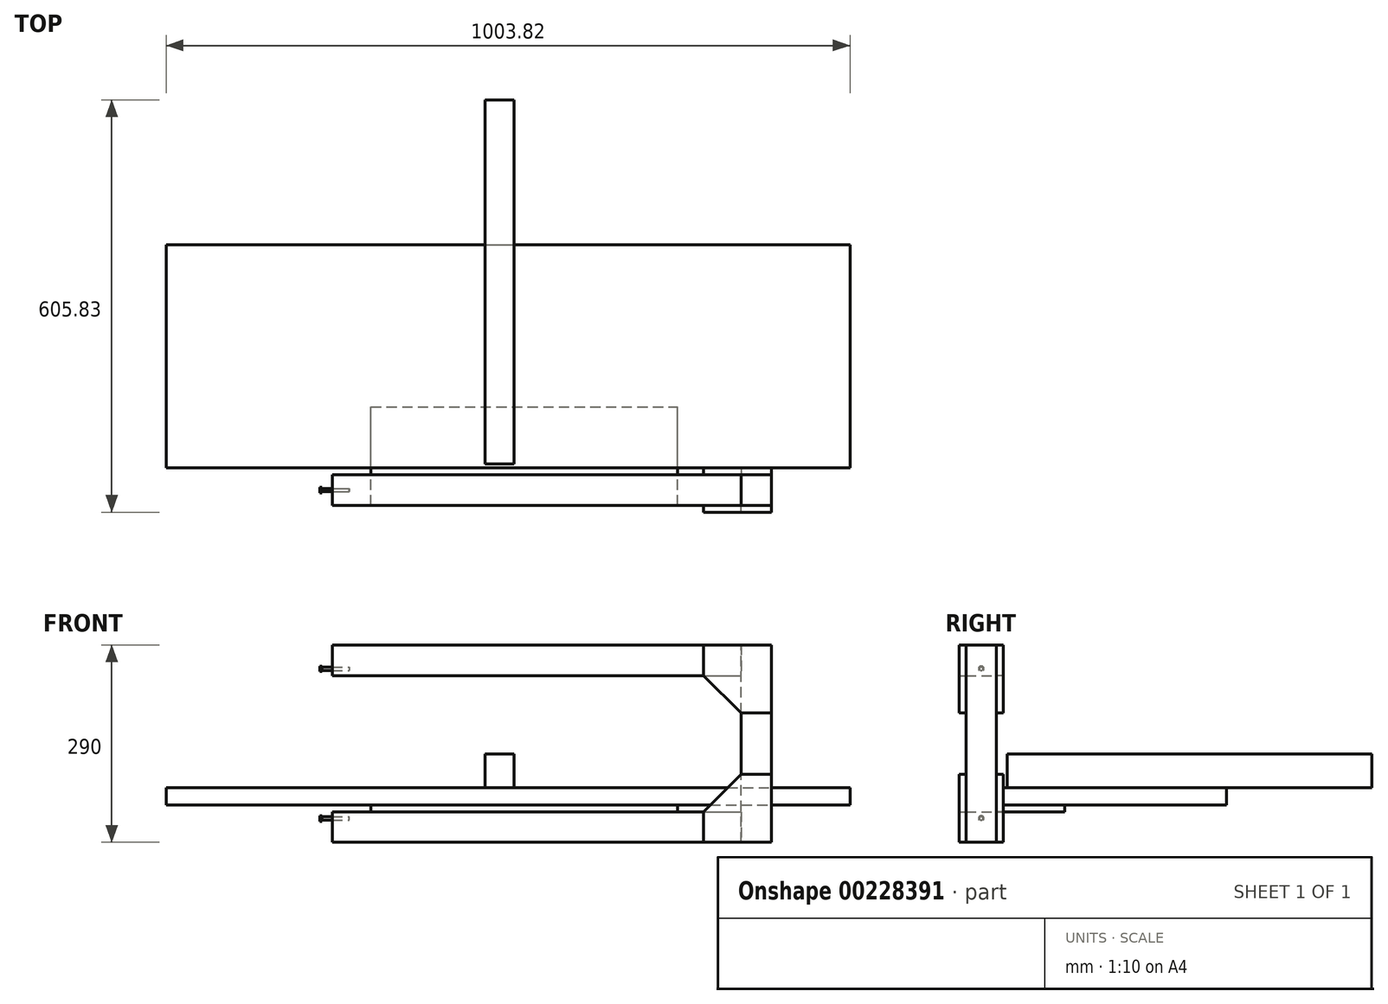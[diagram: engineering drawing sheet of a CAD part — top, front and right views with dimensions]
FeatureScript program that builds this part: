
annotation { "Feature Type Name" : "Feature", "Feature Type Description" : "" }
export const myFeature = defineFeature(function(context is Context, id is Id, definition is map)
    precondition{}
    {
        {
            var Q0;
            Q0=qCreatedBy(makeId("Front.planeOp"),FACE);
            var sketch = newSketch(context, id + "F0", { "sketchPlane" : qUnion([Q0])});
            skLineSegment(sketch, "E0.bottom", {"start": v(22.5, -145) * mm, "end": v(-22.5, -145) * mm});
            skLineSegment(sketch, "E0.top", {"start": v(22.5, 145) * mm, "end": v(-22.5, 145) * mm});
            skLineSegment(sketch, "E0.left", {"start": v(22.5, -145) * mm, "end": v(22.5, 145) * mm});
            skLineSegment(sketch, "E0.right", {"start": v(-22.5, -145) * mm, "end": v(-22.5, 145) * mm});
            skPoint(sketch, "E0.middle", {"position": v(0, 0) * mm});
            skSolve(sketch);
        }
        {
            var Q0;
            Q0 = qSketchRegion(id + "F0", true);
            extrude(context, id + "F1", {"entities" : qUnion([Q0]), "endBound" : BoundingType.SYMMETRIC, "depth" : 45 * mm});
        }
        {
            var Q0;
            Q0=qCreatedBy(makeId("Front.planeOp"),FACE);
            var sketch = newSketch(context, id + "F2", { "sketchPlane" : qUnion([Q0])});
            skLineSegment(sketch, "E1.bottom", {"start": v(-622.5, 145) * mm, "end": v(-22.5, 145) * mm});
            skLineSegment(sketch, "E1.top", {"start": v(-622.5, 100) * mm, "end": v(-22.5, 100) * mm});
            skLineSegment(sketch, "E1.left", {"start": v(-622.5, 145) * mm, "end": v(-622.5, 100) * mm});
            skLineSegment(sketch, "E1.right", {"start": v(-22.5, 145) * mm, "end": v(-22.5, 100) * mm});
            skLineSegment(sketch, "E2.bottom", {"start": v(-622.5, -100) * mm, "end": v(-22.5, -100) * mm});
            skLineSegment(sketch, "E2.top", {"start": v(-622.5, -145) * mm, "end": v(-22.5, -145) * mm});
            skLineSegment(sketch, "E2.left", {"start": v(-622.5, -100) * mm, "end": v(-622.5, -145) * mm});
            skLineSegment(sketch, "E2.right", {"start": v(-22.5, -100) * mm, "end": v(-22.5, -145) * mm});
            skSolve(sketch);
        }
        {
            var Q0;
            Q0 = qSketchRegion(id + "F2", true);
            extrude(context, id + "F3", {"entities" : qUnion([Q0]), "endBound" : BoundingType.SYMMETRIC, "depth" : 45 * mm});
        }
        {
            var Q0;
            Q0=makeQuery(id+"F1.opExtrude","CAP_FACE",FACE,{"disambiguationData":[OSD([sQuery(id+"F0.wireOp",EDGE,"E0.bottom"),sQuery(id+"F0.wireOp",EDGE,"E0.top"),sQuery(id+"F0.wireOp",EDGE,"E0.left"),sQuery(id+"F0.wireOp",EDGE,"E0.right")])],"isStart":false});
            var sketch = newSketch(context, id + "F4", { "sketchPlane" : qUnion([Q0])});
            skLineSegment(sketch, "E3", {"start": v(22.5, -145) * mm, "end": v(22.5, -45) * mm});
            skLineSegment(sketch, "E4", {"start": v(22.5, -45) * mm, "end": v(-22.5, -45) * mm});
            skLineSegment(sketch, "E5", {"start": v(-22.5, -45) * mm, "end": v(-77.5, -100) * mm});
            skLineSegment(sketch, "E6", {"start": v(-77.5, -100) * mm, "end": v(-77.5, -145) * mm});
            skLineSegment(sketch, "E7", {"start": v(-77.5, -145) * mm, "end": v(22.5, -145) * mm});
            skSolve(sketch);
        }
        {
            var Q0;
            Q0 = qSketchRegion(id + "F4", true);
            extrude(context, id + "F5", {"entities" : qUnion([Q0]), "depth" : 10 * mm});
        }
        {
            var Q0;
            Q0=makeQuery(id+"F5.opExtrude","SWEPT_BODY",BODY,{"disambiguationData":[OSD([sQuery(id+"F4.wireOp",EDGE,"E3"),sQuery(id+"F4.wireOp",EDGE,"E4"),sQuery(id+"F4.wireOp",EDGE,"E5"),sQuery(id+"F4.wireOp",EDGE,"E6"),sQuery(id+"F4.wireOp",EDGE,"E7")])]});
            var Q1;
            Q1=qCreatedBy(makeId("Front.planeOp"),FACE);
            mirror(context, id + "F6", {"entities" : qUnion([Q0]), "mirrorPlane" : qUnion([Q1])});
        }
        {
            var Q0;
            Q0=makeQuery(id+"F5.opExtrude","SWEPT_BODY",BODY,{"disambiguationData":[OSD([sQuery(id+"F4.wireOp",EDGE,"E3"),sQuery(id+"F4.wireOp",EDGE,"E4"),sQuery(id+"F4.wireOp",EDGE,"E5"),sQuery(id+"F4.wireOp",EDGE,"E6"),sQuery(id+"F4.wireOp",EDGE,"E7")])]});
            var Q1;
            Q1=makeQuery(id+"F6.opPattern","COPY",BODY,{"derivedFrom":makeQuery(id+"F5.opExtrude","SWEPT_BODY",BODY,{"disambiguationData":[OSD([sQuery(id+"F4.wireOp",EDGE,"E3"),sQuery(id+"F4.wireOp",EDGE,"E4"),sQuery(id+"F4.wireOp",EDGE,"E5"),sQuery(id+"F4.wireOp",EDGE,"E6"),sQuery(id+"F4.wireOp",EDGE,"E7")])]}),"instanceName":"1"});
            var Q2;
            Q2=qCreatedBy(makeId("Top.planeOp"),FACE);
            mirror(context, id + "F7", {"entities" : qUnion([Q0, Q1]), "mirrorPlane" : qUnion([Q2])});
        }
        {
            var Q0;
            Q0=makeQuery(id+"F3.opExtrude","SWEPT_FACE",FACE,{"disambiguationData":[OSD([sQuery(id+"F2.wireOp",EDGE,"E1.left")])]});
            var sketch = newSketch(context, id + "F8", { "sketchPlane" : qUnion([Q0])});
            skCircle(sketch, "E8", {"center": v(0, 110) * mm, "radius": 2.5 * mm});
            skPoint(sketch, "E8.centerSnap0", {"position": v(0, 100) * mm});
            skSolve(sketch);
        }
        {
            var Q0;
            Q0 = qSketchRegion(id + "F8", true);
            extrude(context, id + "F9", {"entities" : qUnion([Q0]), "depth" : 15 * mm, "hasSecondDirection" : true, "secondDirectionOppositeDirection" : true, "secondDirectionDepth" : 25 * mm});
        }
        {
            var Q0;
            Q0=makeQuery(id+"F9.opExtrude","CAP_FACE",FACE,{"disambiguationData":[OSD([sQuery(id+"F8.wireOp",EDGE,"E8")])],"isStart":false});
            var sketch = newSketch(context, id + "F10", { "sketchPlane" : qUnion([Q0])});
            skCircle(sketch, "E9", {"center": v(0, 110) * mm, "radius": 4 * mm});
            skSolve(sketch);
        }
        {
            var Q0;
            Q0 = qSketchRegion(id + "F10", true);
            extrude(context, id + "F11", {"entities" : qUnion([Q0]), "operationType" : NewBodyOperationType.ADD, "depth" : 3 * mm});
        }
        {
            var Q0;
            Q0=makeQuery(id+"F9.opExtrude","SWEPT_BODY",BODY,{"disambiguationData":[OSD([sQuery(id+"F8.wireOp",EDGE,"E8")])]});
            var Q1;
            Q1=qCreatedBy(makeId("Top.planeOp"),FACE);
            mirror(context, id + "F12", {"entities" : qUnion([Q0]), "mirrorPlane" : qUnion([Q1])});
        }
        {
            var Q0;
            Q0=makeQuery(id+"F3.opExtrude","SWEPT_FACE",FACE,{"disambiguationData":[OSD([sQuery(id+"F2.wireOp",EDGE,"E2.bottom")])]});
            var sketch = newSketch(context, id + "F13", { "sketchPlane" : qUnion([Q0])});
            skLineSegment(sketch, "E10.bottom", {"start": v(-565.68, -22.5) * mm, "end": v(-115.68, -22.5) * mm});
            skLineSegment(sketch, "E10.top", {"start": v(-565.68, 122.5) * mm, "end": v(-115.68, 122.5) * mm});
            skLineSegment(sketch, "E10.left", {"start": v(-565.68, -22.5) * mm, "end": v(-565.68, 122.5) * mm});
            skLineSegment(sketch, "E10.right", {"start": v(-115.68, -22.5) * mm, "end": v(-115.68, 122.5) * mm});
            skSolve(sketch);
        }
        {
            var Q0;
            Q0 = qSketchRegion(id + "F13", true);
            extrude(context, id + "F14", {"entities" : qUnion([Q0]), "depth" : 10 * mm});
        }
        {
            var Q0;
            Q0=makeQuery(id+"F14.opExtrude","CAP_FACE",FACE,{"disambiguationData":[OSD([sQuery(id+"F13.wireOp",EDGE,"E10.bottom"),sQuery(id+"F13.wireOp",EDGE,"E10.top"),sQuery(id+"F13.wireOp",EDGE,"E10.left"),sQuery(id+"F13.wireOp",EDGE,"E10.right")])],"isStart":false});
            var sketch = newSketch(context, id + "F15", { "sketchPlane" : qUnion([Q0])});
            skLineSegment(sketch, "E11.bottom", {"start": v(-866.14, 360.23) * mm, "end": v(137.68, 360.23) * mm});
            skLineSegment(sketch, "E11.top", {"start": v(-866.14, 32.5) * mm, "end": v(137.68, 32.5) * mm});
            skLineSegment(sketch, "E11.left", {"start": v(-866.14, 360.23) * mm, "end": v(-866.14, 32.5) * mm});
            skLineSegment(sketch, "E11.right", {"start": v(137.68, 360.23) * mm, "end": v(137.68, 32.5) * mm});
            skSolve(sketch);
        }
        {
            var Q0;
            Q0 = qSketchRegion(id + "F15", true);
            extrude(context, id + "F16", {"entities" : qUnion([Q0]), "depth" : 25 * mm});
        }
        {
            var Q0;
            Q0=makeQuery(id+"F16.opExtrude","CAP_FACE",FACE,{"disambiguationData":[OSD([sQuery(id+"F15.wireOp",EDGE,"E11.bottom"),sQuery(id+"F15.wireOp",EDGE,"E11.top"),sQuery(id+"F15.wireOp",EDGE,"E11.left"),sQuery(id+"F15.wireOp",EDGE,"E11.right")])],"isStart":false});
            var sketch = newSketch(context, id + "F17", { "sketchPlane" : qUnion([Q0])});
            skLineSegment(sketch, "E12.bottom", {"start": v(-398.37, 573.33) * mm, "end": v(-355.58, 573.33) * mm});
            skLineSegment(sketch, "E12.top", {"start": v(-398.37, 38.31) * mm, "end": v(-355.58, 38.31) * mm});
            skLineSegment(sketch, "E12.left", {"start": v(-398.37, 573.33) * mm, "end": v(-398.37, 38.31) * mm});
            skLineSegment(sketch, "E12.right", {"start": v(-355.58, 573.33) * mm, "end": v(-355.58, 38.31) * mm});
            skSolve(sketch);
        }
        {
            var Q0;
            Q0 = qSketchRegion(id + "F17", true);
            extrude(context, id + "F18", {"entities" : qUnion([Q0]), "depth" : 50 * mm});
        }
    });
